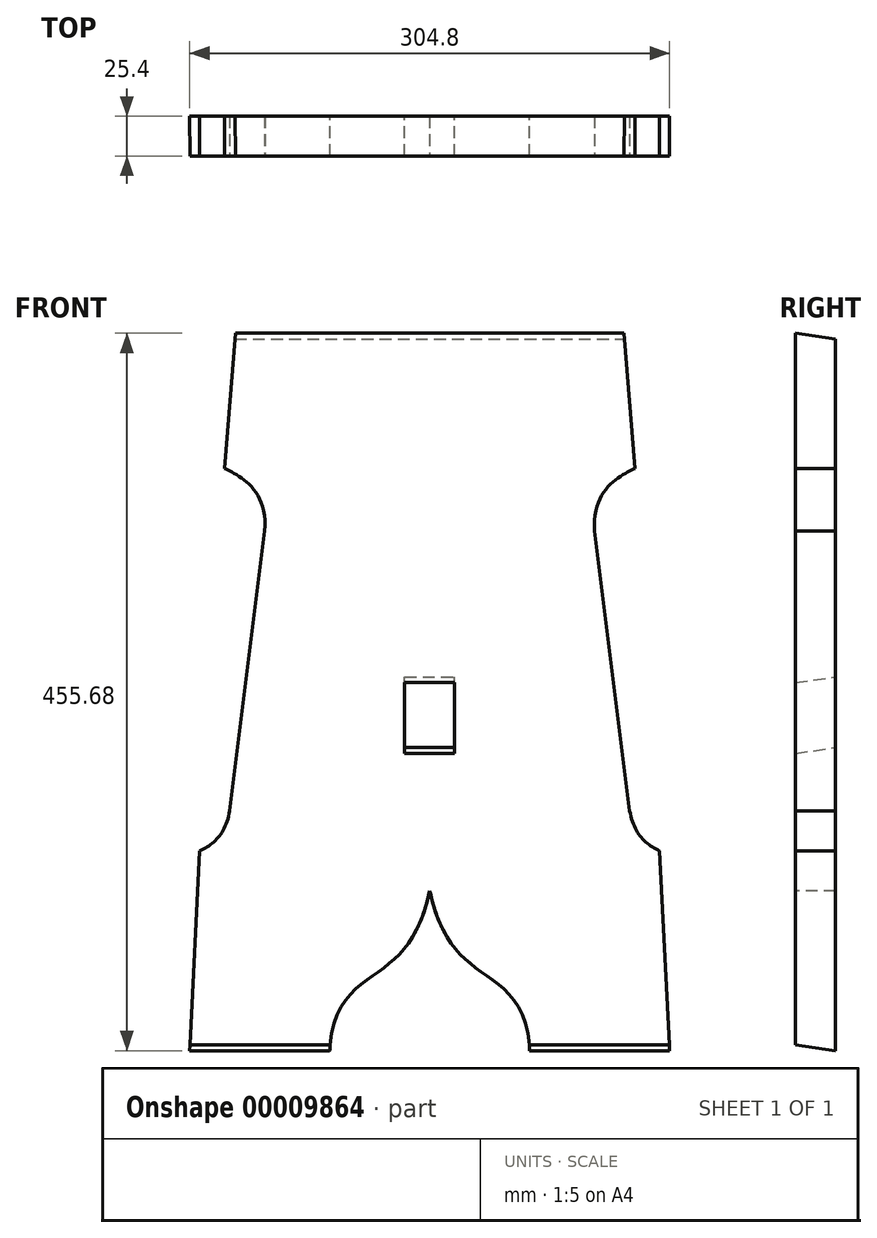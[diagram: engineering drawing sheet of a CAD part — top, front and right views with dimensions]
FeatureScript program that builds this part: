
annotation { "Feature Type Name" : "Feature", "Feature Type Description" : "" }
export const myFeature = defineFeature(function(context is Context, id is Id, definition is map)
    precondition{}
    {
        {
            var Q0;
            Q0=qCreatedBy(makeId("Front.planeOp"),FACE);
            var sketch = newSketch(context, id + "F0", { "sketchPlane" : qUnion([Q0])});
            skLineSegment(sketch, "E0.bottom", {"start": v(-152.4, 227.84) * mm, "end": v(152.4, 227.84) * mm});
            skLineSegment(sketch, "E0.top", {"start": v(-152.4, -227.84) * mm, "end": v(152.4, -227.84) * mm});
            skLineSegment(sketch, "E0.left", {"start": v(-152.4, 227.84) * mm, "end": v(-152.4, -227.84) * mm});
            skLineSegment(sketch, "E0.right", {"start": v(152.4, 227.84) * mm, "end": v(152.4, -227.84) * mm});
            skSolve(sketch);
        }
        {
            var Q0;
            Q0=makeQuery(id+"F0.imprint","IMPRINT",FACE,{"disambiguationData":[TD([[makeQuery(id+"F0.imprint","IMPRINT",EDGE,{"derivedFrom":sQuery(id+"F0.wireOp",EDGE,"E0.bottom")}),-1.0]])]});
            extrude(context, id + "F1", {"entities" : qUnion([Q0]), "depth" : 25.4 * mm});
        }
        {
            var Q0;
            Q0=makeQuery(id+"F1.opExtrude","CAP_FACE",FACE,{"disambiguationData":[OSD([sQuery(id+"F0.wireOp",EDGE,"E0.bottom"),sQuery(id+"F0.wireOp",EDGE,"E0.top"),sQuery(id+"F0.wireOp",EDGE,"E0.left"),sQuery(id+"F0.wireOp",EDGE,"E0.right")])],"isStart":false});
            var sketch = newSketch(context, id + "F2", { "sketchPlane" : qUnion([Q0])});
            skLineSegment(sketch, "E1.0.0", {"start": v(152.4, 227.84) * mm, "end": v(-152.4, 227.84) * mm});
            skLineSegment(sketch, "E1.0.1", {"start": v(-152.4, 227.84) * mm, "end": v(-152.4, -227.84) * mm});
            skLineSegment(sketch, "E1.0.2", {"start": v(-152.4, -227.84) * mm, "end": v(152.4, -227.84) * mm});
            skLineSegment(sketch, "E1.0.3", {"start": v(152.4, -227.84) * mm, "end": v(152.4, 227.84) * mm});
            skPoint(sketch, "E2", {"position": v(-63.5, -227.84) * mm});
            skPoint(sketch, "E3", {"position": v(0, -126.24) * mm});
            skPoint(sketch, "E4", {"position": v(-146.05, -100.84) * mm});
            skFitSpline(sketch, "E5", {"points": [v(0, -126.24) * mm, v(-31.75, -177.04) * mm, v(-63.5, -227.84) * mm], "startDerivative": vector(-39.59, -178.43) * mm, "endDerivative": vector(-7.4, -191.1) * mm});
            skLineSegment(sketch, "E6", {"start": v(0, 227.84) * mm, "end": v(0, -227.84) * mm, "construction": true});
            skFitSpline(sketch, "E7.0.MirrorCS", {"points": [v(0, -126.24) * mm, v(31.75, -177.04) * mm, v(63.5, -227.84) * mm], "startDerivative": vector(39.59, -178.43) * mm, "endDerivative": vector(7.4, -191.1) * mm});
            skLineSegment(sketch, "E8", {"start": v(-146.05, -100.84) * mm, "end": v(-152.4, -227.84) * mm});
            skLineSegment(sketch, "E9.0.MirrorCS", {"start": v(146.05, -100.84) * mm, "end": v(152.4, -227.84) * mm});
            skPoint(sketch, "E10", {"position": v(-127, -75.44) * mm});
            skPoint(sketch, "E11", {"position": v(-114.3, 26.16) * mm});
            skLineSegment(sketch, "E12", {"start": v(-127, -75.44) * mm, "end": v(-114.3, 26.16) * mm});
            skLineSegment(sketch, "E13", {"start": v(-114.3, 26.16) * mm, "end": v(-104.78, 102.36) * mm});
            skFitSpline(sketch, "E14", {"points": [v(-146.05, -100.84) * mm, v(-127, -75.44) * mm], "startDerivative": vector(28.37, 12.36) * mm, "endDerivative": vector(7.56, 42.49) * mm});
            skPoint(sketch, "E15", {"position": v(-104.78, 102.36) * mm});
            skPoint(sketch, "E16", {"position": v(-114.3, 127.76) * mm});
            skPoint(sketch, "E17", {"position": v(-127, 140.46) * mm});
            skFitSpline(sketch, "E18", {"points": [v(-104.78, 102.36) * mm, v(-130.25, 142.06) * mm], "startDerivative": vector(7.33, 82.79) * mm, "endDerivative": vector(-20.35, 10.96) * mm});
            skLineSegment(sketch, "E19", {"start": v(-130.25, 142.06) * mm, "end": v(-123.47, 227.84) * mm});
            skLineSegment(sketch, "E20.0.MirrorCS", {"start": v(130.25, 142.06) * mm, "end": v(123.47, 227.84) * mm});
            skFitSpline(sketch, "E21.0.MirrorCS", {"points": [v(104.78, 102.36) * mm, v(130.25, 142.06) * mm], "startDerivative": vector(-7.33, 82.79) * mm, "endDerivative": vector(20.35, 10.96) * mm});
            skLineSegment(sketch, "E22.0.MirrorCS", {"start": v(114.3, 26.16) * mm, "end": v(104.77, 102.36) * mm});
            skLineSegment(sketch, "E23.0.MirrorCS", {"start": v(127, -75.44) * mm, "end": v(114.3, 26.16) * mm});
            skFitSpline(sketch, "E24.0.MirrorCS", {"points": [v(146.05, -100.84) * mm, v(127, -75.44) * mm], "startDerivative": vector(-28.37, 12.36) * mm, "endDerivative": vector(-7.56, 42.49) * mm});
            skSolve(sketch);
        }
        {
            var Q0;
            {var subQ1=sQuery(id+"F2.wireOp",EDGE,"E1.0.1");Q0=makeQuery(id+"F2.imprint","IMPRINT",FACE,{"disambiguationData":[TD([[makeQuery(id+"F2.imprint","IMPRINT",EDGE,{"derivedFrom":subQ1}),1.0]])]});}
            var Q1;
            {var subQ1=sQuery(id+"F2.wireOp",EDGE,"E5");Q1=makeQuery(id+"F2.imprint","IMPRINT",FACE,{"disambiguationData":[TD([[makeQuery(id+"F2.imprint","IMPRINT",EDGE,{"derivedFrom":subQ1}),1.0]])]});}
            var Q2;
            {var subQ1=sQuery(id+"F2.wireOp",EDGE,"E1.0.3");Q2=makeQuery(id+"F2.imprint","IMPRINT",FACE,{"disambiguationData":[TD([[makeQuery(id+"F2.imprint","IMPRINT",EDGE,{"derivedFrom":subQ1}),-1.0]])]});}
            extrude(context, id + "F3", {"entities" : qUnion([Q0, Q1, Q2]), "operationType" : NewBodyOperationType.REMOVE, "endBound" : BoundingType.THROUGH_ALL, "oppositeDirection" : true, "depth" : 25.4 * mm});
        }
        {
            var Q0;
            Q0=qCreatedBy(makeId("Right.planeOp"),FACE);
            cPlane(context, id + "F4", {"entities" : qUnion([Q0]), "cplaneType" : CPlaneType.OFFSET, "offset" : 152.4 * mm, "width" : 152.4 * mm, "height" : 152.4 * mm});
        }
        {
            var Q0;
            Q0=qCreatedBy(id+"F4.planeOp",FACE);
            var sketch = newSketch(context, id + "F5", { "sketchPlane" : qUnion([Q0])});
            skLineSegment(sketch, "E25.0.0", {"start": v(0, -100.84) * mm, "end": v(-25.4, -100.84) * mm});
            skLineSegment(sketch, "E25.0.1", {"start": v(-25.4, -100.84) * mm, "end": v(-25.4, -227.84) * mm});
            skLineSegment(sketch, "E25.0.2", {"start": v(-25.4, -227.84) * mm, "end": v(0, -227.84) * mm});
            skLineSegment(sketch, "E25.0.3", {"start": v(0, -227.84) * mm, "end": v(0, -100.84) * mm});
            skLineSegment(sketch, "E26", {"start": v(0, -227.84) * mm, "end": v(-25.4, -224.08) * mm});
            skLineSegment(sketch, "E27.0.0", {"start": v(0, 142.06) * mm, "end": v(0, 227.84) * mm});
            skLineSegment(sketch, "E27.0.1", {"start": v(0, 227.84) * mm, "end": v(-25.4, 227.84) * mm});
            skLineSegment(sketch, "E27.0.2", {"start": v(-25.4, 227.84) * mm, "end": v(-25.4, 142.06) * mm});
            skLineSegment(sketch, "E27.0.3", {"start": v(-25.4, 142.06) * mm, "end": v(0, 142.06) * mm});
            skLineSegment(sketch, "E28", {"start": v(-25.4, 227.84) * mm, "end": v(0, 224.08) * mm});
            skSolve(sketch);
        }
        {
            var Q0;
            {var subQ1=sQuery(id+"F5.wireOp",EDGE,"E27.0.1");Q0=makeQuery(id+"F5.imprint","IMPRINT",FACE,{"disambiguationData":[TD([[makeQuery(id+"F5.imprint","IMPRINT",EDGE,{"derivedFrom":subQ1}),1.0]])]});}
            var Q1;
            {var subQ1=sQuery(id+"F5.wireOp",EDGE,"E25.0.2");Q1=makeQuery(id+"F5.imprint","IMPRINT",FACE,{"disambiguationData":[TD([[makeQuery(id+"F5.imprint","IMPRINT",EDGE,{"derivedFrom":subQ1}),1.0]])]});}
            extrude(context, id + "F6", {"entities" : qUnion([Q0, Q1]), "operationType" : NewBodyOperationType.REMOVE, "endBound" : BoundingType.THROUGH_ALL, "oppositeDirection" : true, "depth" : 25.4 * mm});
        }
        {
            var Q0;
            Q0=qCreatedBy(makeId("Right.planeOp"),FACE);
            var sketch = newSketch(context, id + "F7", { "sketchPlane" : qUnion([Q0])});
            skLineSegment(sketch, "E29", {"start": v(0, 0) * mm, "end": v(-9.74, 65.82) * mm});
            skLineSegment(sketch, "E30", {"start": v(0, 0) * mm, "end": v(-25, 0) * mm, "construction": true});
            skSolve(sketch);
        }
        {
            var Q0;
            Q0=sQuery(id+"F7.wireOp",EDGE,"E29");
            cPlane(context, id + "F8", {"entities" : qUnion([Q0]), "cplaneType" : CPlaneType.LINE_ANGLE, "offset" : 152.4 * mm, "angle" : 90 * degree, "width" : 152.4 * mm, "height" : 152.4 * mm});
        }
        {
            var Q0;
            Q0=qCreatedBy(id+"F8.planeOp",FACE);
            cPlane(context, id + "F9", {"entities" : qUnion([Q0]), "cplaneType" : CPlaneType.OFFSET, "offset" : 25.4 * mm, "width" : 152.4 * mm, "height" : 152.4 * mm});
        }
        {
            var Q0;
            Q0=qCreatedBy(id+"F9.planeOp",FACE);
            var sketch = newSketch(context, id + "F10", { "sketchPlane" : qUnion([Q0])});
            skLineSegment(sketch, "E31.0.0", {"start": v(130.25, 140.53) * mm, "end": v(123.77, 221.66) * mm});
            skLineSegment(sketch, "E31.0.1", {"start": v(123.77, 221.66) * mm, "end": v(-123.77, 221.66) * mm});
            skLineSegment(sketch, "E31.0.2", {"start": v(-123.77, 221.66) * mm, "end": v(-130.25, 140.53) * mm});
            skFitSpline(sketch, "E31.0.3", {"points": [v(-130.25, 140.53) * mm, v(-123.47, 136.92) * mm, v(-102.33, 128.56) * mm, v(-104.78, 101.26) * mm]});
            skLineSegment(sketch, "E31.0.4", {"start": v(-104.77, 101.26) * mm, "end": v(-127, -74.62) * mm});
            skFitSpline(sketch, "E31.0.5", {"points": [v(-127, -74.62) * mm, v(-129.52, -88.63) * mm, v(-136.6, -95.67) * mm, v(-146.05, -99.75) * mm]});
            skLineSegment(sketch, "E31.0.6", {"start": v(-146.05, -99.75) * mm, "end": v(-152.4, -225.38) * mm});
            skLineSegment(sketch, "E31.0.7", {"start": v(-152.4, -225.38) * mm, "end": v(-63.5, -225.38) * mm});
            skFitSpline(sketch, "E31.0.8", {"points": [v(-63.5, -225.38) * mm, v(-62.27, -193.88) * mm, v(-29.07, -176.17) * mm, v(-6.6, -154.3) * mm, v(0, -124.88) * mm]});
            skFitSpline(sketch, "E31.0.9", {"points": [v(0, -124.88) * mm, v(6.6, -154.3) * mm, v(29.07, -176.17) * mm, v(62.27, -193.88) * mm, v(63.5, -225.38) * mm]});
            skLineSegment(sketch, "E31.0.10", {"start": v(63.5, -225.38) * mm, "end": v(152.4, -225.38) * mm});
            skLineSegment(sketch, "E31.0.11", {"start": v(152.4, -225.38) * mm, "end": v(146.05, -99.75) * mm});
            skFitSpline(sketch, "E31.0.12", {"points": [v(146.05, -99.75) * mm, v(136.6, -95.67) * mm, v(129.52, -88.63) * mm, v(127, -74.62) * mm]});
            skLineSegment(sketch, "E31.0.13", {"start": v(127, -74.62) * mm, "end": v(104.78, 101.26) * mm});
            skFitSpline(sketch, "E31.0.14", {"points": [v(104.78, 101.26) * mm, v(102.33, 128.56) * mm, v(123.47, 136.92) * mm, v(130.25, 140.53) * mm]});
            skLineSegment(sketch, "E32.bottom", {"start": v(-15.88, 9.57) * mm, "end": v(15.88, 9.57) * mm});
            skLineSegment(sketch, "E32.top", {"start": v(-15.87, -34.88) * mm, "end": v(15.88, -34.88) * mm});
            skLineSegment(sketch, "E32.left", {"start": v(-15.88, 9.57) * mm, "end": v(-15.87, -34.88) * mm});
            skLineSegment(sketch, "E32.right", {"start": v(15.88, 9.57) * mm, "end": v(15.88, -34.88) * mm});
            skSolve(sketch);
        }
        {
            var Q0;
            Q0=makeQuery(id+"F10.imprint","IMPRINT",FACE,{"disambiguationData":[TD([[makeQuery(id+"F10.imprint","IMPRINT",EDGE,{"derivedFrom":sQuery(id+"F10.wireOp",EDGE,"E32.bottom")}),-1.0]])]});
            extrude(context, id + "F11", {"entities" : qUnion([Q0]), "operationType" : NewBodyOperationType.REMOVE, "endBound" : BoundingType.THROUGH_ALL, "oppositeDirection" : true, "depth" : 25.4 * mm});
        }
    });
